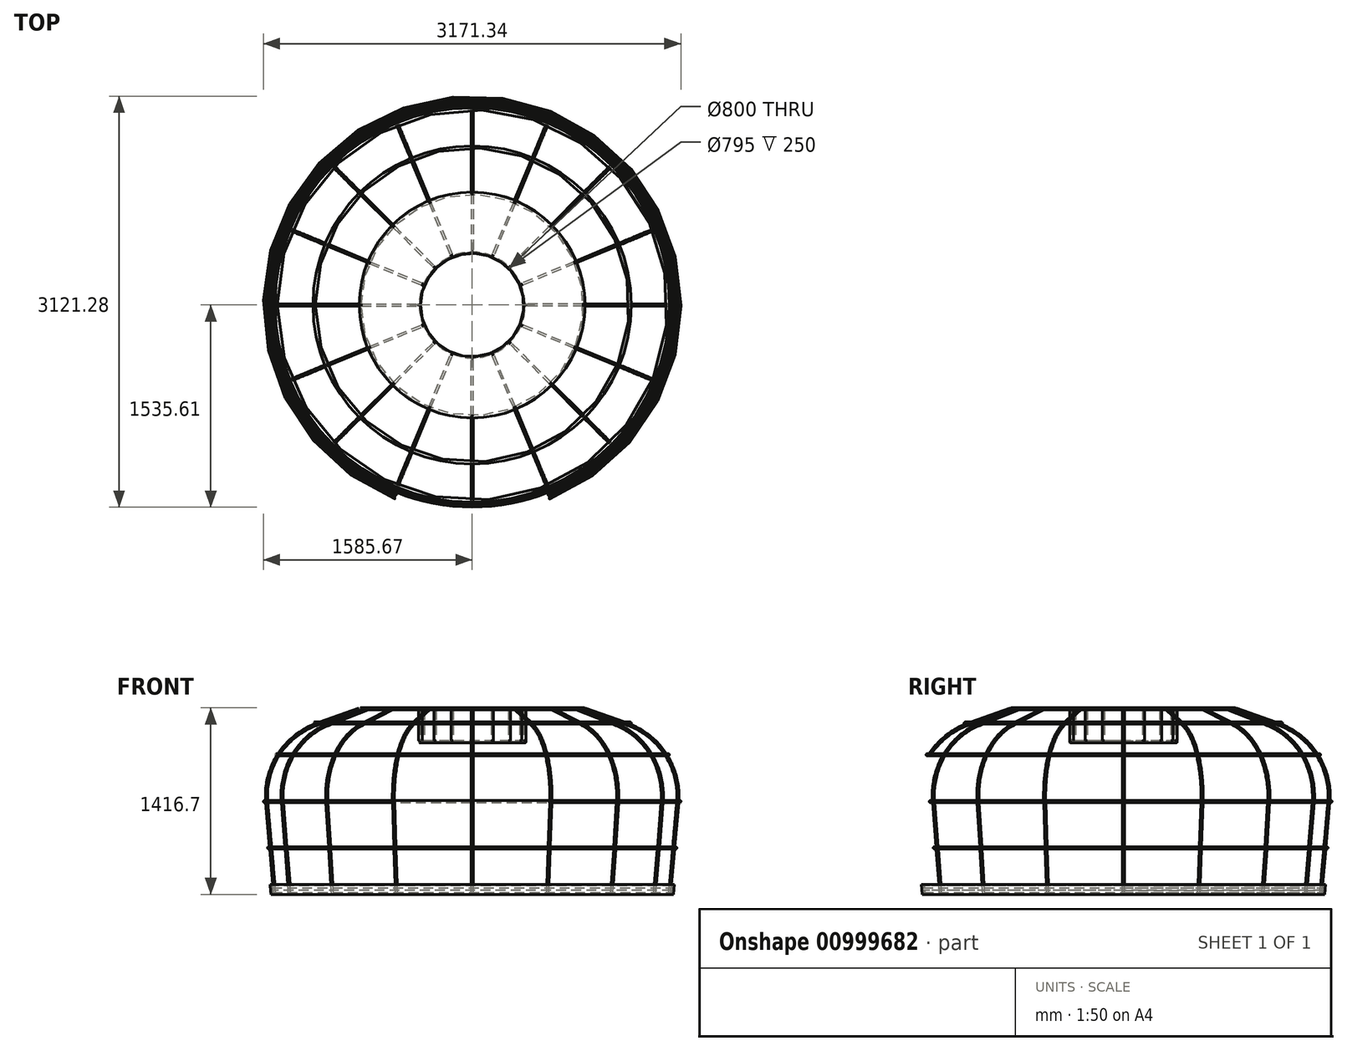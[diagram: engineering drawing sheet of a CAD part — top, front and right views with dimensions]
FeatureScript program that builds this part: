
annotation { "Feature Type Name" : "Feature", "Feature Type Description" : "" }
export const myFeature = defineFeature(function(context is Context, id is Id, definition is map)
    precondition{}
    {
        {
            var Q0;
            Q0=qCreatedBy(makeId("Front.planeOp"),FACE);
            var sketch = newSketch(context, id + "F0", { "sketchPlane" : qUnion([Q0])});
            skLineSegment(sketch, "E0", {"start": v(-1500, 0) * mm, "end": v(1500, 0) * mm, "construction": true});
            skLineSegment(sketch, "E1", {"start": v(-1500, 0) * mm, "end": v(-1561, 697.34) * mm});
            skLineSegment(sketch, "E2", {"start": v(0, 0) * mm, "end": v(0, 1400) * mm, "construction": true});
            skLineSegment(sketch, "E3", {"start": v(-400, 1416) * mm, "end": v(-850, 1416) * mm});
            skLineSegment(sketch, "E4", {"start": v(-850, 1416) * mm, "end": v(-850, 1400) * mm, "construction": true});
            skLineSegment(sketch, "E5", {"start": v(-850, 1400) * mm, "end": v(-400, 1400) * mm});
            skLineSegment(sketch, "E6", {"start": v(-400, 1400) * mm, "end": v(-400, 1416) * mm, "construction": true});
            skLineSegment(sketch, "E7", {"start": v(-858, 1408) * mm, "end": v(-1183.81, 1289.41) * mm});
            skArc(sketch, "E8", {"start": v(-1183.81, 1289.41) * mm, "mid": v(-1472.9, 1057.4) * mm, "end": v(-1561, 697.34) * mm});
            skCircle(sketch, "E9", {"center": v(-400, 1408) * mm, "radius": 8 * mm});
            skCircle(sketch, "E10", {"center": v(-850, 1408) * mm, "radius": 8 * mm});
            skCircle(sketch, "E11", {"center": v(-1500, 0) * mm, "radius": 8 * mm});
            skLineSegment(sketch, "E12", {"start": v(-400, 1408) * mm, "end": v(-400, 1158) * mm, "construction": true});
            skCircle(sketch, "E13", {"center": v(-400, 1158) * mm, "radius": 8 * mm});
            skLineSegment(sketch, "E14", {"start": v(-850, 1408) * mm, "end": v(-400, 1408) * mm, "construction": true});
            skPoint(sketch, "E15", {"position": v(-842, 1408) * mm});
            skPoint(sketch, "E16", {"position": v(-408, 1408) * mm});
            skPoint(sketch, "E17", {"position": v(-400, 1166) * mm});
            skLineSegment(sketch, "E18", {"start": v(-850, 1408) * mm, "end": v(-858, 1408) * mm, "construction": true});
            skPoint(sketch, "E19", {"position": v(-1500.7, 7.97) * mm});
            skSolve(sketch);
        }
        {
            var Q0;
            Q0=makeQuery(id+"F0.imprint","IMPRINT",FACE,{"disambiguationData":[TD([[makeQuery(id+"F0.imprint","IMPRINT",EDGE,{"derivedFrom":sQuery(id+"F0.wireOp",EDGE,"E13")}),1.0]])]});
            var Q1;
            {var subQ0=sQuery(id+"F0.wireOp",EDGE,"E9");var subQ1=makeQuery(id+"F0.imprint","INTERSECT",VERTEX,{"derivedFrom":[sQuery(id+"F0.wireOp",EDGE,"E3"),subQ0]});Q1=makeQuery(id+"F0.imprint","IMPRINT",FACE,{"disambiguationData":[TD([[makeQuery(id+"F0.imprint","IMPRINT",EDGE,{"disambiguationData":[TD([[subQ1,-1.0]])],"derivedFrom":subQ0}),1.0]])]});}
            var Q2;
            {var subQ0=sQuery(id+"F0.wireOp",EDGE,"E10");var subQ2=makeQuery(id+"F0.imprint","IMPRINT",VERTEX,{"derivedFrom":subQ0});Q2=makeQuery(id+"F0.imprint","IMPRINT",FACE,{"disambiguationData":[TD([[makeQuery(id+"F0.imprint","IMPRINT",EDGE,{"disambiguationData":[TD([[subQ2,1.0]])],"derivedFrom":subQ0}),1.0]])]});}
            var Q3;
            Q3=sQuery(id+"F0.wireOp",EDGE,"E11");
            var Q4;
            Q4=sQuery(id+"F0.wireOp",EDGE,"E10");
            var Q5;
            Q5=sQuery(id+"F0.wireOp",EDGE,"E9");
            var Q6;
            Q6=sQuery(id+"F0.wireOp",EDGE,"E13");
            var Q7;
            Q7=sQuery(id+"F0.wireOp",EDGE,"E2");
            revolve(context, id + "F1", {"surfaceOperationType" : NewSurfaceOperationType.NEW, "entities" : qUnion([Q0, Q1, Q2]), "surfaceEntities" : qUnion([Q3, Q4, Q5, Q6]), "axis" : qUnion([Q7]), "revolveType" : RevolveType.FULL});
        }
        {
            var Q0;
            Q0=sQuery(id+"F0.wireOp",EDGE,"E14");
            var Q1;
            Q1=qCreatedBy(makeId("Top.planeOp"),FACE);
            cPlane(context, id + "F2", {"entities" : qUnion([Q0, Q1]), "cplaneType" : CPlaneType.LINE_ANGLE, "offset" : 25 * mm, "angle" : 0 * degree, "width" : 150 * mm, "height" : 150 * mm});
        }
        {
            var Q0;
            Q0=sQuery(id+"F0.wireOp",VERTEX,"E16");
            var Q1;
            Q1=qCreatedBy(makeId("Right.planeOp"),FACE);
            cPlane(context, id + "F3", {"entities" : qUnion([Q0, Q1]), "cplaneType" : CPlaneType.PLANE_POINT, "offset" : 25 * mm, "width" : 150 * mm, "height" : 150 * mm});
        }
        {
            var Q0;
            Q0=qCreatedBy(id+"F3.planeOp",FACE);
            var sketch = newSketch(context, id + "F4", { "sketchPlane" : qUnion([Q0])});
            skCircle(sketch, "E20", {"center": v(0, 1408) * mm, "radius": 8 * mm});
            skSolve(sketch);
        }
        {
            var Q0;
            Q0=qSketchRegion(id+"F4",true);
            var Q1;
            Q1=makeQuery(id+"F1.opRevolve","SWEPT_FACE",FACE,{"disambiguationData":[OSD([sQuery(id+"F0.wireOp",EDGE,"E10")])]});
            var Q2;
            Q2=sQuery(id+"F0.wireOp",VERTEX,"E15");
            extrude(context, id + "F5", {"entities" : qUnion([Q0]), "endBound" : BoundingType.UP_TO_VERTEX, "oppositeDirection" : true, "depth" : 25 * mm, "endBoundEntityFace" : qUnion([Q1]), "endBoundEntityVertex" : qUnion([Q2]), "offsetDistance" : 25 * mm});
        }
        {
            var Q0;
            Q0=sQuery(id+"F0.wireOp",VERTEX,"E17");
            var Q1;
            Q1=qCreatedBy(makeId("Top.planeOp"),FACE);
            cPlane(context, id + "F6", {"entities" : qUnion([Q0, Q1]), "cplaneType" : CPlaneType.PLANE_POINT, "offset" : 25 * mm, "width" : 150 * mm, "height" : 150 * mm});
        }
        {
            var Q0;
            Q0=qCreatedBy(id+"F6.planeOp",FACE);
            var sketch = newSketch(context, id + "F7", { "sketchPlane" : qUnion([Q0])});
            skCircle(sketch, "E21", {"center": v(-400, 0) * mm, "radius": 8 * mm});
            skSolve(sketch);
        }
        {
            var Q0;
            Q0=qSketchRegion(id+"F7",true);
            var Q1;
            Q1=sQuery(id+"F0.wireOp",VERTEX,"E5.end");
            extrude(context, id + "F8", {"entities" : qUnion([Q0]), "endBound" : BoundingType.UP_TO_VERTEX, "depth" : 25 * mm, "endBoundEntityVertex" : qUnion([Q1]), "offsetDistance" : 25 * mm});
        }
        {
            var Q0;
            Q0=makeQuery(id+"F8.opExtrude","SWEPT_BODY",BODY,{"disambiguationData":[OSD([sQuery(id+"F7.wireOp",EDGE,"E21")])]});
            var Q1;
            Q1=makeQuery(id+"F5.opExtrude","SWEPT_BODY",BODY,{"disambiguationData":[OSD([sQuery(id+"F4.wireOp",EDGE,"E20")])]});
            var Q2;
            Q2=sQuery(id+"F0.wireOp",EDGE,"E2");
            circularPattern(context, id + "F9", {"entities" : qUnion([Q0, Q1]), "axis" : qUnion([Q2]), "angle" : 360 * degree, "instanceCount" : 16, "equalSpace" : true});
        }
        {
            var Q0;
            Q0=sQuery(id+"F0.wireOp",VERTEX,"E0.start");
            var Q1;
            Q1=sQuery(id+"F0.wireOp",EDGE,"E1");
            cPlane(context, id + "F10", {"entities" : qUnion([Q0, Q1]), "cplaneType" : CPlaneType.LINE_POINT, "offset" : 25 * mm, "width" : 150 * mm, "height" : 150 * mm});
        }
        {
            var Q0;
            Q0=qCreatedBy(id+"F10.planeOp",FACE);
            var sketch = newSketch(context, id + "F11", { "sketchPlane" : qUnion([Q0])});
            skCircle(sketch, "E22", {"center": v(-1494.3, 0) * mm, "radius": 8 * mm});
            skSolve(sketch);
        }
        {
            var Q0;
            Q0=makeQuery(id+"F11.imprint","IMPRINT",FACE,{"disambiguationData":[TD([[makeQuery(id+"F11.imprint","IMPRINT",EDGE,{"derivedFrom":sQuery(id+"F11.wireOp",EDGE,"E22")}),1.0]])]});
            var Q1;
            Q1=sQuery(id+"F0.wireOp",EDGE,"E1");
            var Q2;
            Q2=sQuery(id+"F0.wireOp",EDGE,"E8");
            var Q3;
            Q3=sQuery(id+"F0.wireOp",EDGE,"E7");
            sweep(context, id + "F12", {"profiles" : qUnion([Q0]), "path" : qUnion([Q1, Q2, Q3])});
        }
        {
            var Q0;
            Q0=makeQuery(id+"F12.opSweep","SWEPT_BODY",BODY,{"disambiguationData":[OSD([sQuery(id+"F0.wireOp",EDGE,"E7"),sQuery(id+"F11.wireOp",EDGE,"E22")])]});
            var Q1;
            Q1=sQuery(id+"F0.wireOp",EDGE,"E2");
            circularPattern(context, id + "F13", {"entities" : qUnion([Q0]), "axis" : qUnion([Q1]), "angle" : 360 * degree, "instanceCount" : 16, "equalSpace" : true});
        }
        {
            var Q0;
            Q0=qCreatedBy(makeId("Front.planeOp"),FACE);
            var sketch = newSketch(context, id + "F14", { "sketchPlane" : qUnion([Q0])});
            skCircle(sketch, "E23", {"center": v(-1577.67, 705) * mm, "radius": 8 * mm});
            skArc(sketch, "E24.0", {"start": v(-1183.81, 1289.41) * mm, "mid": v(-1472.9, 1057.4) * mm, "end": v(-1561, 697.34) * mm, "construction": true});
            skPoint(sketch, "E24.2", {"position": v(-1472.9, 1057.4) * mm});
            skArc(sketch, "E25.0", {"start": v(-1186.55, 1296.93) * mm, "mid": v(-1479.65, 1061.7) * mm, "end": v(-1568.98, 696.64) * mm, "construction": true});
            skLineSegment(sketch, "E26.0", {"start": v(-1508.03, 0) * mm, "end": v(-1568.98, 696.64) * mm, "construction": true});
            skCircle(sketch, "E27", {"center": v(-1546.94, 353) * mm, "radius": 8 * mm});
            skCircle(sketch, "E28", {"center": v(-1490.16, 1060) * mm, "radius": 8 * mm});
            skCircle(sketch, "E29", {"center": v(-1201.11, 1300) * mm, "radius": 8 * mm});
            skLineSegment(sketch, "E30.0", {"start": v(-860.74, 1415.52) * mm, "end": v(-1186.55, 1296.93) * mm, "construction": true});
            skSolve(sketch);
        }
        {
            var Q0;
            Q0=makeQuery(id+"F14.imprint","IMPRINT",FACE,{"disambiguationData":[TD([[makeQuery(id+"F14.imprint","IMPRINT",EDGE,{"derivedFrom":sQuery(id+"F14.wireOp",EDGE,"E23")}),1.0]])]});
            var Q1;
            Q1=makeQuery(id+"F14.imprint","IMPRINT",FACE,{"disambiguationData":[TD([[makeQuery(id+"F14.imprint","IMPRINT",EDGE,{"derivedFrom":sQuery(id+"F14.wireOp",EDGE,"E27")}),1.0]])]});
            var Q2;
            Q2=makeQuery(id+"F14.imprint","IMPRINT",FACE,{"disambiguationData":[TD([[makeQuery(id+"F14.imprint","IMPRINT",EDGE,{"derivedFrom":sQuery(id+"F14.wireOp",EDGE,"E28")}),1.0]])]});
            var Q3;
            Q3=makeQuery(id+"F14.imprint","IMPRINT",FACE,{"disambiguationData":[TD([[makeQuery(id+"F14.imprint","IMPRINT",EDGE,{"derivedFrom":sQuery(id+"F14.wireOp",EDGE,"E29")}),1.0]])]});
            var Q4;
            Q4=sQuery(id+"F0.wireOp",EDGE,"E2");
            revolve(context, id + "F15", {"surfaceOperationType" : NewSurfaceOperationType.NEW, "entities" : qUnion([Q0, Q1, Q2, Q3]), "axis" : qUnion([Q4]), "revolveType" : RevolveType.FULL});
        }
        {
            var Q0;
            Q0=qCreatedBy(makeId("Front.planeOp"),FACE);
            var sketch = newSketch(context, id + "F16", { "sketchPlane" : qUnion([Q0])});
            skLineSegment(sketch, "E31", {"start": v(-588.37, 715.59) * mm, "end": v(-576.32, 342.94) * mm});
            skLineSegment(sketch, "E32", {"start": v(-576.32, 342.94) * mm, "end": v(-9.37, 9.13) * mm});
            skLineSegment(sketch, "E33", {"start": v(-9.37, 9.13) * mm, "end": v(9.02, 9.13) * mm});
            skLineSegment(sketch, "E34", {"start": v(9.02, 9.13) * mm, "end": v(576.23, 342.85) * mm});
            skLineSegment(sketch, "E35", {"start": v(576.23, 342.85) * mm, "end": v(585.83, 715.98) * mm});
            skLineSegment(sketch, "E36", {"start": v(585.83, 715.98) * mm, "end": v(9.02, 1051.53) * mm});
            skLineSegment(sketch, "E37", {"start": v(9.02, 1051.53) * mm, "end": v(-8.88, 1051.53) * mm});
            skLineSegment(sketch, "E38", {"start": v(-8.88, 1051.53) * mm, "end": v(-588.37, 715.59) * mm});
            skSolve(sketch);
        }
        {
            var Q0;
            Q0 = qSketchRegion(id + "F16", true);
            extrude(context, id + "F17", {"entities" : qUnion([Q0]), "operationType" : NewBodyOperationType.REMOVE, "endBound" : BoundingType.THROUGH_ALL, "depth" : 25 * mm, "offsetDistance" : 25 * mm});
        }
        {
            var Q0;
            Q0=qCreatedBy(id+"F2.planeOp",FACE);
            var sketch = newSketch(context, id + "F18", { "sketchPlane" : qUnion([Q0])});
            skCircle(sketch, "E39", {"center": v(0, 0) * mm, "radius": 850 * mm});
            skCircle(sketch, "E40", {"center": v(0, 0) * mm, "radius": 400 * mm});
            skSolve(sketch);
        }
        {
            var Q0;
            Q0 = qSketchRegion(id + "F18", true);
            extrude(context, id + "F19", {"entities" : qUnion([Q0]), "depth" : 5 * mm, "offsetDistance" : 25 * mm, "symmetric" : true});
        }
        {
            var Q0;
            Q0=qCreatedBy(makeId("Front.planeOp"),FACE);
            var sketch = newSketch(context, id + "F20", { "sketchPlane" : qUnion([Q0])});
            skLineSegment(sketch, "E41.0", {"start": v(-397.5, 1410) * mm, "end": v(-397.5, 1160) * mm});
            skLineSegment(sketch, "E42.0", {"start": v(-402.5, 1410) * mm, "end": v(-402.5, 1160) * mm});
            skLineSegment(sketch, "E43", {"start": v(-402.5, 1160) * mm, "end": v(-397.5, 1160) * mm});
            skLineSegment(sketch, "E44", {"start": v(-402.5, 1410) * mm, "end": v(-397.5, 1410) * mm});
            skSolve(sketch);
        }
        {
            var Q0;
            Q0 = qSketchRegion(id + "F20", true);
            var Q1;
            Q1=sQuery(id+"F0.wireOp",EDGE,"E2");
            revolve(context, id + "F21", {"surfaceOperationType" : NewSurfaceOperationType.NEW, "entities" : qUnion([Q0]), "axis" : qUnion([Q1]), "revolveType" : RevolveType.FULL});
        }
        {
            var Q0;
            Q0=qCreatedBy(makeId("Front.planeOp"),FACE);
            var sketch = newSketch(context, id + "F22", { "sketchPlane" : qUnion([Q0])});
            skCircle(sketch, "E45", {"center": v(-1517.86, 20.52) * mm, "radius": 8 * mm});
            skCircle(sketch, "E46", {"center": v(-1520.9, 55.39) * mm, "radius": 8 * mm});
            skLineSegment(sketch, "E47.0", {"start": v(-1508.03, 0) * mm, "end": v(-1568.98, 696.64) * mm, "construction": true});
            skLineSegment(sketch, "E48", {"start": v(-1508.03, 0) * mm, "end": v(-1524.1, 0) * mm, "construction": true});
            skLineSegment(sketch, "E49", {"start": v(-1524.1, 0) * mm, "end": v(-1530.63, 74.71) * mm, "construction": true});
            skSolve(sketch);
        }
        {
            var Q0;
            Q0 = qSketchRegion(id + "F22", true);
            var Q1;
            Q1=sQuery(id+"F0.wireOp",EDGE,"E2");
            revolve(context, id + "F23", {"surfaceOperationType" : NewSurfaceOperationType.NEW, "entities" : qUnion([Q0]), "axis" : qUnion([Q1]), "revolveType" : RevolveType.FULL});
        }
        {
            var Q0;
            Q0=qCreatedBy(makeId("Front.planeOp"),FACE);
            var sketch = newSketch(context, id + "F24", { "sketchPlane" : qUnion([Q0])});
            skLineSegment(sketch, "E50.0", {"start": v(-1524.1, 0) * mm, "end": v(-1530.63, 74.71) * mm});
            skLineSegment(sketch, "E51", {"start": v(-1530.63, 74.71) * mm, "end": v(-1535.6, 74.28) * mm});
            skLineSegment(sketch, "E52", {"start": v(-1535.6, 74.28) * mm, "end": v(-1529.07, -0.44) * mm});
            skLineSegment(sketch, "E53", {"start": v(-1529.07, -0.44) * mm, "end": v(-1524.1, 0) * mm});
            skSolve(sketch);
        }
        {
            var Q0;
            Q0 = qSketchRegion(id + "F24", true);
            var Q1;
            Q1=sQuery(id+"F0.wireOp",EDGE,"E2");
            revolve(context, id + "F25", {"surfaceOperationType" : NewSurfaceOperationType.NEW, "entities" : qUnion([Q0]), "axis" : qUnion([Q1]), "revolveType" : RevolveType.FULL});
        }
    });
